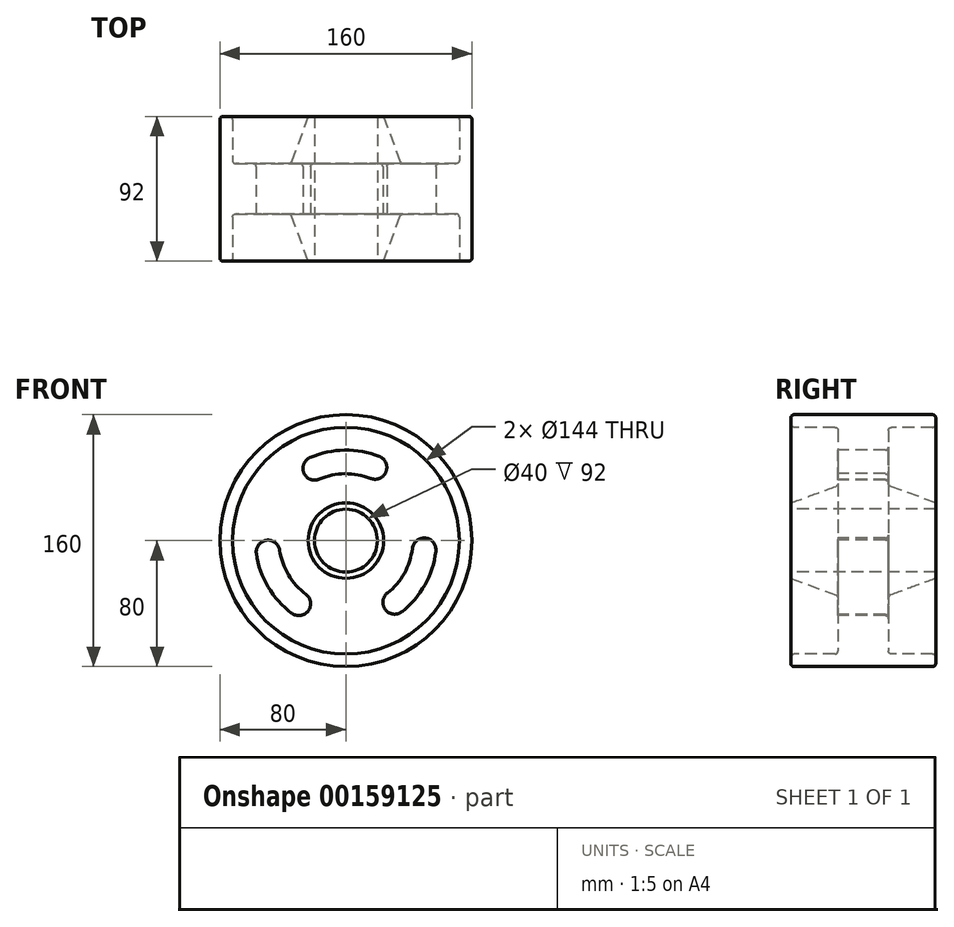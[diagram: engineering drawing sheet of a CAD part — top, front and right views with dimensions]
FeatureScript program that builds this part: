
annotation { "Feature Type Name" : "Feature", "Feature Type Description" : "" }
export const myFeature = defineFeature(function(context is Context, id is Id, definition is map)
    precondition{}
    {
        {
            var Q0;
            Q0=qCreatedBy(makeId("Right.planeOp"),FACE);
            var sketch = newSketch(context, id + "F0", { "sketchPlane" : qUnion([Q0])});
            skLineSegment(sketch, "E0.bottom", {"start": v(0, 0) * mm, "end": v(92, 0) * mm});
            skLineSegment(sketch, "E0.top", {"start": v(0, 80) * mm, "end": v(92, 80) * mm});
            skLineSegment(sketch, "E0.left", {"start": v(0, 0) * mm, "end": v(0, 80) * mm});
            skLineSegment(sketch, "E0.right", {"start": v(92, 0) * mm, "end": v(92, 80) * mm});
            skLineSegment(sketch, "E1", {"start": v(0, 72) * mm, "end": v(30, 72) * mm});
            skLineSegment(sketch, "E2", {"start": v(30, 72) * mm, "end": v(30, 35) * mm});
            skLineSegment(sketch, "E3", {"start": v(30, 35) * mm, "end": v(0, 24) * mm});
            skLineSegment(sketch, "E4", {"start": v(0, 24) * mm, "end": v(0, 20) * mm});
            skLineSegment(sketch, "E5", {"start": v(0, 20) * mm, "end": v(92, 20) * mm});
            skLineSegment(sketch, "E6", {"start": v(0, 80) * mm, "end": v(0, 72) * mm});
            skLineSegment(sketch, "E7", {"start": v(92, 80) * mm, "end": v(92, 72) * mm});
            skLineSegment(sketch, "E8", {"start": v(92, 72) * mm, "end": v(62, 72) * mm});
            skLineSegment(sketch, "E9", {"start": v(62, 72) * mm, "end": v(62, 35) * mm});
            skLineSegment(sketch, "E10", {"start": v(62, 35) * mm, "end": v(92, 24) * mm});
            skLineSegment(sketch, "E11", {"start": v(92, 24) * mm, "end": v(92, 20) * mm});
            skLineSegment(sketch, "E12", {"start": v(-62.89, 0) * mm, "end": v(165.3, 0) * mm, "construction": true});
            skSolve(sketch);
        }
        {
            var Q0;
            Q0=makeQuery(id+"F0.imprint","IMPRINT",FACE,{"disambiguationData":[TD([[makeQuery(id+"F0.imprint","IMPRINT",EDGE,{"derivedFrom":sQuery(id+"F0.wireOp",EDGE,"E1")}),1.0]])]});
            var Q1;
            Q1=sQuery(id+"F0.wireOp",EDGE,"E12");
            revolve(context, id + "F1", {"entities" : qUnion([Q0]), "axis" : qUnion([Q1]), "revolveType" : RevolveType.FULL});
        }
        {
            var Q0;
            Q0=makeQuery(id+"F1.opRevolve","SWEPT_FACE",FACE,{"disambiguationData":[OSD([sQuery(id+"F0.wireOp",EDGE,"E2")])]});
            var sketch = newSketch(context, id + "F2", { "sketchPlane" : qUnion([Q0])});
            skCircle(sketch, "E13", {"center": v(0, 0) * mm, "radius": 50 * mm, "construction": true});
            skCircle(sketch, "E14", {"center": v(-19.76, 45.93) * mm, "radius": 7.5 * mm});
            skCircle(sketch, "E15", {"center": v(18.5, 46.45) * mm, "radius": 7.5 * mm});
            skCircle(sketch, "E16", {"center": v(49.66, -5.85) * mm, "radius": 7.5 * mm});
            skCircle(sketch, "E17", {"center": v(30.98, -39.25) * mm, "radius": 7.5 * mm});
            skCircle(sketch, "E18", {"center": v(-49.48, -7.2) * mm, "radius": 7.5 * mm});
            skCircle(sketch, "E19", {"center": v(-29.9, -40.08) * mm, "radius": 7.5 * mm});
            skLineSegment(sketch, "E20", {"start": v(-19.76, 45.93) * mm, "end": v(0, 0) * mm, "construction": true});
            skLineSegment(sketch, "E21", {"start": v(18.5, 46.45) * mm, "end": v(0, 0) * mm, "construction": true});
            skLineSegment(sketch, "E22", {"start": v(49.66, -5.85) * mm, "end": v(0, 0) * mm, "construction": true});
            skLineSegment(sketch, "E23", {"start": v(30.98, -39.25) * mm, "end": v(0, 0) * mm, "construction": true});
            skLineSegment(sketch, "E24", {"start": v(-29.9, -40.08) * mm, "end": v(0, 0) * mm, "construction": true});
            skLineSegment(sketch, "E25", {"start": v(-49.48, -7.2) * mm, "end": v(0, 0) * mm, "construction": true});
            skCircle(sketch, "E26", {"center": v(0, 0) * mm, "radius": 57.5 * mm});
            skCircle(sketch, "E27", {"center": v(0, 0) * mm, "radius": 42.5 * mm});
            skSolve(sketch);
        }
        {
            var Q0;
            {var subQ0=sQuery(id+"F2.wireOp",EDGE,"E26");var subQ1=sQuery(id+"F2.wireOp",EDGE,"E14");var subQ2=makeQuery(id+"F2.imprint","INTERSECT",VERTEX,{"derivedFrom":[subQ1,subQ0]});Q0=makeQuery(id+"F2.imprint","IMPRINT",FACE,{"disambiguationData":[TD([[makeQuery(id+"F2.imprint","IMPRINT",EDGE,{"disambiguationData":[TD([[subQ2,1.0]])],"derivedFrom":subQ1}),-1.0]])]});}
            var Q1;
            {var subQ0=sQuery(id+"F2.wireOp",EDGE,"E15");var subQ1=makeQuery(id+"F2.imprint","INTERSECT",VERTEX,{"derivedFrom":[subQ0,sQuery(id+"F2.wireOp",EDGE,"E26")]});Q1=makeQuery(id+"F2.imprint","IMPRINT",FACE,{"disambiguationData":[TD([[makeQuery(id+"F2.imprint","IMPRINT",EDGE,{"disambiguationData":[TD([[subQ1,-1.0]])],"derivedFrom":subQ0}),1.0]])]});}
            var Q2;
            {var subQ0=sQuery(id+"F2.wireOp",EDGE,"E14");var subQ1=makeQuery(id+"F2.imprint","INTERSECT",VERTEX,{"derivedFrom":[subQ0,sQuery(id+"F2.wireOp",EDGE,"E26")]});Q2=makeQuery(id+"F2.imprint","IMPRINT",FACE,{"disambiguationData":[TD([[makeQuery(id+"F2.imprint","IMPRINT",EDGE,{"disambiguationData":[TD([[subQ1,-1.0]])],"derivedFrom":subQ0}),1.0]])]});}
            var Q3;
            {var subQ0=sQuery(id+"F2.wireOp",EDGE,"E26");var subQ1=sQuery(id+"F2.wireOp",EDGE,"E18");var subQ2=makeQuery(id+"F2.imprint","INTERSECT",VERTEX,{"derivedFrom":[subQ1,subQ0]});Q3=makeQuery(id+"F2.imprint","IMPRINT",FACE,{"disambiguationData":[TD([[makeQuery(id+"F2.imprint","IMPRINT",EDGE,{"disambiguationData":[TD([[subQ2,-1.0]])],"derivedFrom":subQ1}),-1.0]])]});}
            var Q4;
            {var subQ0=sQuery(id+"F2.wireOp",EDGE,"E19");var subQ1=makeQuery(id+"F2.imprint","INTERSECT",VERTEX,{"derivedFrom":[subQ0,sQuery(id+"F2.wireOp",EDGE,"E26")]});Q4=makeQuery(id+"F2.imprint","IMPRINT",FACE,{"disambiguationData":[TD([[makeQuery(id+"F2.imprint","IMPRINT",EDGE,{"disambiguationData":[TD([[subQ1,1.0]])],"derivedFrom":subQ0}),1.0]])]});}
            var Q5;
            {var subQ0=sQuery(id+"F2.wireOp",EDGE,"E18");var subQ1=makeQuery(id+"F2.imprint","INTERSECT",VERTEX,{"derivedFrom":[subQ0,sQuery(id+"F2.wireOp",EDGE,"E26")]});Q5=makeQuery(id+"F2.imprint","IMPRINT",FACE,{"disambiguationData":[TD([[makeQuery(id+"F2.imprint","IMPRINT",EDGE,{"disambiguationData":[TD([[subQ1,1.0]])],"derivedFrom":subQ0}),1.0]])]});}
            var Q6;
            {var subQ0=sQuery(id+"F2.wireOp",EDGE,"E26");var subQ1=sQuery(id+"F2.wireOp",EDGE,"E16");var subQ2=makeQuery(id+"F2.imprint","INTERSECT",VERTEX,{"derivedFrom":[subQ1,subQ0]});Q6=makeQuery(id+"F2.imprint","IMPRINT",FACE,{"disambiguationData":[TD([[makeQuery(id+"F2.imprint","IMPRINT",EDGE,{"disambiguationData":[TD([[subQ2,1.0]])],"derivedFrom":subQ1}),-1.0]])]});}
            var Q7;
            {var subQ0=sQuery(id+"F2.wireOp",EDGE,"E16");var subQ1=makeQuery(id+"F2.imprint","INTERSECT",VERTEX,{"derivedFrom":[subQ0,sQuery(id+"F2.wireOp",EDGE,"E26")]});Q7=makeQuery(id+"F2.imprint","IMPRINT",FACE,{"disambiguationData":[TD([[makeQuery(id+"F2.imprint","IMPRINT",EDGE,{"disambiguationData":[TD([[subQ1,1.0]])],"derivedFrom":subQ0}),1.0]])]});}
            var Q8;
            {var subQ0=sQuery(id+"F2.wireOp",EDGE,"E17");var subQ1=makeQuery(id+"F2.imprint","INTERSECT",VERTEX,{"derivedFrom":[subQ0,sQuery(id+"F2.wireOp",EDGE,"E26")]});Q8=makeQuery(id+"F2.imprint","IMPRINT",FACE,{"disambiguationData":[TD([[makeQuery(id+"F2.imprint","IMPRINT",EDGE,{"disambiguationData":[TD([[subQ1,1.0]])],"derivedFrom":subQ0}),1.0]])]});}
            extrude(context, id + "F3", {"entities" : qUnion([Q0, Q1, Q2, Q3, Q4, Q5, Q6, Q7, Q8]), "operationType" : NewBodyOperationType.REMOVE, "endBound" : BoundingType.THROUGH_ALL, "oppositeDirection" : true, "depth" : 25 * mm});
        }
        {
            var Q0;
            Q0=makeQuery(id+"F1.opRevolve","SWEPT_EDGE",EDGE,{"disambiguationData":[OSD([sQuery(id+"F0.wireOp",EDGE,"E6"),sQuery(id+"F0.wireOp",EDGE,"E0.top")])]});
            var Q1;
            Q1=makeQuery(id+"F1.opRevolve","SWEPT_EDGE",EDGE,{"disambiguationData":[OSD([sQuery(id+"F0.wireOp",EDGE,"E0.left"),sQuery(id+"F0.wireOp",EDGE,"E1"),sQuery(id+"F0.wireOp",EDGE,"E6")])]});
            var Q2;
            Q2=makeQuery(id+"F1.opRevolve","SWEPT_EDGE",EDGE,{"disambiguationData":[OSD([sQuery(id+"F0.wireOp",EDGE,"E2"),sQuery(id+"F0.wireOp",EDGE,"E3")])]});
            var Q3;
            Q3=makeQuery(id+"F3.boolean.opBoolean","COPY",EDGE,{"derivedFrom":makeQuery(id+"F3.opExtrude","CAP_EDGE",EDGE,{"disambiguationData":[OSD([sQuery(id+"F2.wireOp",EDGE,"E15")])],"isStart":true})});
            var Q4;
            {var subQ0=sQuery(id+"F2.wireOp",EDGE,"E27");Q4=makeQuery(id+"F3.boolean.opBoolean","COPY",EDGE,{"derivedFrom":makeQuery(id+"F3.opExtrude","CAP_EDGE",EDGE,{"disambiguationData":[OSD([subQ0]),TDD([makeQuery(id+"F2.imprint","IMPRINT",EDGE,{"disambiguationData":[TD([[makeQuery(id+"F2.imprint","INTERSECT",VERTEX,{"derivedFrom":[sQuery(id+"F2.wireOp",EDGE,"E14"),subQ0]}),1.0]])],"derivedFrom":subQ0})])],"isStart":true})});}
            var Q5;
            Q5=makeQuery(id+"F3.boolean.opBoolean","COPY",EDGE,{"derivedFrom":makeQuery(id+"F3.opExtrude","CAP_EDGE",EDGE,{"disambiguationData":[OSD([sQuery(id+"F2.wireOp",EDGE,"E14")])],"isStart":true})});
            var Q6;
            {var subQ0=sQuery(id+"F2.wireOp",EDGE,"E26");Q6=makeQuery(id+"F3.boolean.opBoolean","COPY",EDGE,{"derivedFrom":makeQuery(id+"F3.opExtrude","CAP_EDGE",EDGE,{"disambiguationData":[OSD([subQ0]),TDD([makeQuery(id+"F2.imprint","IMPRINT",EDGE,{"disambiguationData":[TD([[makeQuery(id+"F2.imprint","INTERSECT",VERTEX,{"derivedFrom":[sQuery(id+"F2.wireOp",EDGE,"E14"),subQ0]}),1.0]])],"derivedFrom":subQ0})])],"isStart":true})});}
            var Q7;
            Q7=makeQuery(id+"F3.boolean.opBoolean","COPY",EDGE,{"derivedFrom":makeQuery(id+"F3.opExtrude","CAP_EDGE",EDGE,{"disambiguationData":[OSD([sQuery(id+"F2.wireOp",EDGE,"E16")])],"isStart":true})});
            var Q8;
            {var subQ0=sQuery(id+"F2.wireOp",EDGE,"E26");Q8=makeQuery(id+"F3.boolean.opBoolean","COPY",EDGE,{"derivedFrom":makeQuery(id+"F3.opExtrude","CAP_EDGE",EDGE,{"disambiguationData":[OSD([subQ0]),TDD([makeQuery(id+"F2.imprint","IMPRINT",EDGE,{"disambiguationData":[TD([[makeQuery(id+"F2.imprint","INTERSECT",VERTEX,{"derivedFrom":[sQuery(id+"F2.wireOp",EDGE,"E16"),subQ0]}),1.0]])],"derivedFrom":subQ0})])],"isStart":true})});}
            var Q9;
            {var subQ0=sQuery(id+"F2.wireOp",EDGE,"E27");Q9=makeQuery(id+"F3.boolean.opBoolean","COPY",EDGE,{"derivedFrom":makeQuery(id+"F3.opExtrude","CAP_EDGE",EDGE,{"disambiguationData":[OSD([subQ0]),TDD([makeQuery(id+"F2.imprint","IMPRINT",EDGE,{"disambiguationData":[TD([[makeQuery(id+"F2.imprint","INTERSECT",VERTEX,{"derivedFrom":[sQuery(id+"F2.wireOp",EDGE,"E16"),subQ0]}),1.0]])],"derivedFrom":subQ0})])],"isStart":true})});}
            var Q10;
            Q10=makeQuery(id+"F3.boolean.opBoolean","COPY",EDGE,{"derivedFrom":makeQuery(id+"F3.opExtrude","CAP_EDGE",EDGE,{"disambiguationData":[OSD([sQuery(id+"F2.wireOp",EDGE,"E17")])],"isStart":true})});
            var Q11;
            {var subQ0=sQuery(id+"F2.wireOp",EDGE,"E27");Q11=makeQuery(id+"F3.boolean.opBoolean","COPY",EDGE,{"derivedFrom":makeQuery(id+"F3.opExtrude","CAP_EDGE",EDGE,{"disambiguationData":[OSD([subQ0]),TDD([makeQuery(id+"F2.imprint","IMPRINT",EDGE,{"disambiguationData":[TD([[makeQuery(id+"F2.imprint","INTERSECT",VERTEX,{"derivedFrom":[sQuery(id+"F2.wireOp",EDGE,"E18"),subQ0]}),-1.0]])],"derivedFrom":subQ0})])],"isStart":true})});}
            var Q12;
            Q12=makeQuery(id+"F3.boolean.opBoolean","COPY",EDGE,{"derivedFrom":makeQuery(id+"F3.opExtrude","CAP_EDGE",EDGE,{"disambiguationData":[OSD([sQuery(id+"F2.wireOp",EDGE,"E19")])],"isStart":true})});
            var Q13;
            {var subQ0=sQuery(id+"F2.wireOp",EDGE,"E26");Q13=makeQuery(id+"F3.boolean.opBoolean","COPY",EDGE,{"derivedFrom":makeQuery(id+"F3.opExtrude","CAP_EDGE",EDGE,{"disambiguationData":[OSD([subQ0]),TDD([makeQuery(id+"F2.imprint","IMPRINT",EDGE,{"disambiguationData":[TD([[makeQuery(id+"F2.imprint","INTERSECT",VERTEX,{"derivedFrom":[sQuery(id+"F2.wireOp",EDGE,"E18"),subQ0]}),-1.0]])],"derivedFrom":subQ0})])],"isStart":true})});}
            var Q14;
            Q14=makeQuery(id+"F3.boolean.opBoolean","COPY",EDGE,{"derivedFrom":makeQuery(id+"F3.opExtrude","CAP_EDGE",EDGE,{"disambiguationData":[OSD([sQuery(id+"F2.wireOp",EDGE,"E18")])],"isStart":true})});
            var Q15;
            Q15=makeQuery(id+"F1.opRevolve","SWEPT_EDGE",EDGE,{"disambiguationData":[OSD([sQuery(id+"F0.wireOp",EDGE,"E0.top"),sQuery(id+"F0.wireOp",EDGE,"E7")])]});
            var Q16;
            Q16=makeQuery(id+"F1.opRevolve","SWEPT_EDGE",EDGE,{"disambiguationData":[OSD([sQuery(id+"F0.wireOp",EDGE,"E0.right"),sQuery(id+"F0.wireOp",EDGE,"E7"),sQuery(id+"F0.wireOp",EDGE,"E8")])]});
            var Q17;
            {var subQ0=sQuery(id+"F2.wireOp",EDGE,"E26");Q17=makeQuery(id+"F3.boolean.opBoolean","INTERSECT",EDGE,{"derivedFrom":[makeQuery(id+"F1.opRevolve","SWEPT_FACE",FACE,{"disambiguationData":[OSD([sQuery(id+"F0.wireOp",EDGE,"E9")])]}),makeQuery(id+"F3.opExtrude","SWEPT_FACE",FACE,{"disambiguationData":[OSD([subQ0]),TDD([makeQuery(id+"F2.imprint","IMPRINT",EDGE,{"disambiguationData":[TD([[makeQuery(id+"F2.imprint","INTERSECT",VERTEX,{"derivedFrom":[sQuery(id+"F2.wireOp",EDGE,"E14"),subQ0]}),1.0]])],"derivedFrom":subQ0})])]})]});}
            var Q18;
            Q18=makeQuery(id+"F3.boolean.opBoolean","INTERSECT",EDGE,{"derivedFrom":[makeQuery(id+"F1.opRevolve","SWEPT_FACE",FACE,{"disambiguationData":[OSD([sQuery(id+"F0.wireOp",EDGE,"E9")])]}),makeQuery(id+"F3.opExtrude","SWEPT_FACE",FACE,{"disambiguationData":[OSD([sQuery(id+"F2.wireOp",EDGE,"E14")])]})]});
            var Q19;
            Q19=makeQuery(id+"F3.boolean.opBoolean","INTERSECT",EDGE,{"derivedFrom":[makeQuery(id+"F1.opRevolve","SWEPT_FACE",FACE,{"disambiguationData":[OSD([sQuery(id+"F0.wireOp",EDGE,"E9")])]}),makeQuery(id+"F3.opExtrude","SWEPT_FACE",FACE,{"disambiguationData":[OSD([sQuery(id+"F2.wireOp",EDGE,"E15")])]})]});
            var Q20;
            {var subQ0=sQuery(id+"F2.wireOp",EDGE,"E27");Q20=makeQuery(id+"F3.boolean.opBoolean","INTERSECT",EDGE,{"derivedFrom":[makeQuery(id+"F1.opRevolve","SWEPT_FACE",FACE,{"disambiguationData":[OSD([sQuery(id+"F0.wireOp",EDGE,"E9")])]}),makeQuery(id+"F3.opExtrude","SWEPT_FACE",FACE,{"disambiguationData":[OSD([subQ0]),TDD([makeQuery(id+"F2.imprint","IMPRINT",EDGE,{"disambiguationData":[TD([[makeQuery(id+"F2.imprint","INTERSECT",VERTEX,{"derivedFrom":[sQuery(id+"F2.wireOp",EDGE,"E14"),subQ0]}),1.0]])],"derivedFrom":subQ0})])]})]});}
            var Q21;
            Q21=makeQuery(id+"F1.opRevolve","SWEPT_EDGE",EDGE,{"disambiguationData":[OSD([sQuery(id+"F0.wireOp",EDGE,"E9"),sQuery(id+"F0.wireOp",EDGE,"E10")])]});
            var Q22;
            {var subQ0=sQuery(id+"F2.wireOp",EDGE,"E26");Q22=makeQuery(id+"F3.boolean.opBoolean","INTERSECT",EDGE,{"derivedFrom":[makeQuery(id+"F1.opRevolve","SWEPT_FACE",FACE,{"disambiguationData":[OSD([sQuery(id+"F0.wireOp",EDGE,"E9")])]}),makeQuery(id+"F3.opExtrude","SWEPT_FACE",FACE,{"disambiguationData":[OSD([subQ0]),TDD([makeQuery(id+"F2.imprint","IMPRINT",EDGE,{"disambiguationData":[TD([[makeQuery(id+"F2.imprint","INTERSECT",VERTEX,{"derivedFrom":[sQuery(id+"F2.wireOp",EDGE,"E18"),subQ0]}),-1.0]])],"derivedFrom":subQ0})])]})]});}
            var Q23;
            Q23=makeQuery(id+"F3.boolean.opBoolean","INTERSECT",EDGE,{"derivedFrom":[makeQuery(id+"F1.opRevolve","SWEPT_FACE",FACE,{"disambiguationData":[OSD([sQuery(id+"F0.wireOp",EDGE,"E9")])]}),makeQuery(id+"F3.opExtrude","SWEPT_FACE",FACE,{"disambiguationData":[OSD([sQuery(id+"F2.wireOp",EDGE,"E18")])]})]});
            var Q24;
            Q24=makeQuery(id+"F3.boolean.opBoolean","INTERSECT",EDGE,{"derivedFrom":[makeQuery(id+"F1.opRevolve","SWEPT_FACE",FACE,{"disambiguationData":[OSD([sQuery(id+"F0.wireOp",EDGE,"E9")])]}),makeQuery(id+"F3.opExtrude","SWEPT_FACE",FACE,{"disambiguationData":[OSD([sQuery(id+"F2.wireOp",EDGE,"E19")])]})]});
            var Q25;
            {var subQ0=sQuery(id+"F2.wireOp",EDGE,"E27");Q25=makeQuery(id+"F3.boolean.opBoolean","INTERSECT",EDGE,{"derivedFrom":[makeQuery(id+"F1.opRevolve","SWEPT_FACE",FACE,{"disambiguationData":[OSD([sQuery(id+"F0.wireOp",EDGE,"E9")])]}),makeQuery(id+"F3.opExtrude","SWEPT_FACE",FACE,{"disambiguationData":[OSD([subQ0]),TDD([makeQuery(id+"F2.imprint","IMPRINT",EDGE,{"disambiguationData":[TD([[makeQuery(id+"F2.imprint","INTERSECT",VERTEX,{"derivedFrom":[sQuery(id+"F2.wireOp",EDGE,"E18"),subQ0]}),-1.0]])],"derivedFrom":subQ0})])]})]});}
            var Q26;
            Q26=makeQuery(id+"F3.boolean.opBoolean","INTERSECT",EDGE,{"derivedFrom":[makeQuery(id+"F1.opRevolve","SWEPT_FACE",FACE,{"disambiguationData":[OSD([sQuery(id+"F0.wireOp",EDGE,"E9")])]}),makeQuery(id+"F3.opExtrude","SWEPT_FACE",FACE,{"disambiguationData":[OSD([sQuery(id+"F2.wireOp",EDGE,"E17")])]})]});
            var Q27;
            {var subQ0=sQuery(id+"F2.wireOp",EDGE,"E26");Q27=makeQuery(id+"F3.boolean.opBoolean","INTERSECT",EDGE,{"derivedFrom":[makeQuery(id+"F1.opRevolve","SWEPT_FACE",FACE,{"disambiguationData":[OSD([sQuery(id+"F0.wireOp",EDGE,"E9")])]}),makeQuery(id+"F3.opExtrude","SWEPT_FACE",FACE,{"disambiguationData":[OSD([subQ0]),TDD([makeQuery(id+"F2.imprint","IMPRINT",EDGE,{"disambiguationData":[TD([[makeQuery(id+"F2.imprint","INTERSECT",VERTEX,{"derivedFrom":[sQuery(id+"F2.wireOp",EDGE,"E16"),subQ0]}),1.0]])],"derivedFrom":subQ0})])]})]});}
            var Q28;
            Q28=makeQuery(id+"F3.boolean.opBoolean","INTERSECT",EDGE,{"derivedFrom":[makeQuery(id+"F1.opRevolve","SWEPT_FACE",FACE,{"disambiguationData":[OSD([sQuery(id+"F0.wireOp",EDGE,"E9")])]}),makeQuery(id+"F3.opExtrude","SWEPT_FACE",FACE,{"disambiguationData":[OSD([sQuery(id+"F2.wireOp",EDGE,"E16")])]})]});
            var Q29;
            {var subQ0=sQuery(id+"F2.wireOp",EDGE,"E27");Q29=makeQuery(id+"F3.boolean.opBoolean","INTERSECT",EDGE,{"derivedFrom":[makeQuery(id+"F1.opRevolve","SWEPT_FACE",FACE,{"disambiguationData":[OSD([sQuery(id+"F0.wireOp",EDGE,"E9")])]}),makeQuery(id+"F3.opExtrude","SWEPT_FACE",FACE,{"disambiguationData":[OSD([subQ0]),TDD([makeQuery(id+"F2.imprint","IMPRINT",EDGE,{"disambiguationData":[TD([[makeQuery(id+"F2.imprint","INTERSECT",VERTEX,{"derivedFrom":[sQuery(id+"F2.wireOp",EDGE,"E16"),subQ0]}),1.0]])],"derivedFrom":subQ0})])]})]});}
            fillet(context, id + "F4", {"entities" : qUnion([Q0, Q1, Q2, Q3, Q4, Q5, Q6, Q7, Q8, Q9, Q10, Q11, Q12, Q13, Q14, Q15, Q16, Q17, Q18, Q19, Q20, Q21, Q22, Q23, Q24, Q25, Q26, Q27, Q28, Q29]), "radius" : 2 * mm, "tangentPropagation" : true, "allowEdgeOverflow" : false});
        }
        {
            var Q0;
            Q0=makeQuery(id+"F1.opRevolve","SWEPT_EDGE",EDGE,{"disambiguationData":[OSD([sQuery(id+"F0.wireOp",EDGE,"E1"),sQuery(id+"F0.wireOp",EDGE,"E2")])]});
            var Q1;
            Q1=makeQuery(id+"F1.opRevolve","SWEPT_EDGE",EDGE,{"disambiguationData":[OSD([sQuery(id+"F0.wireOp",EDGE,"E8"),sQuery(id+"F0.wireOp",EDGE,"E9")])]});
            fillet(context, id + "F5", {"entities" : qUnion([Q0, Q1]), "radius" : 2 * mm, "tangentPropagation" : true, "allowEdgeOverflow" : false});
        }
    });
